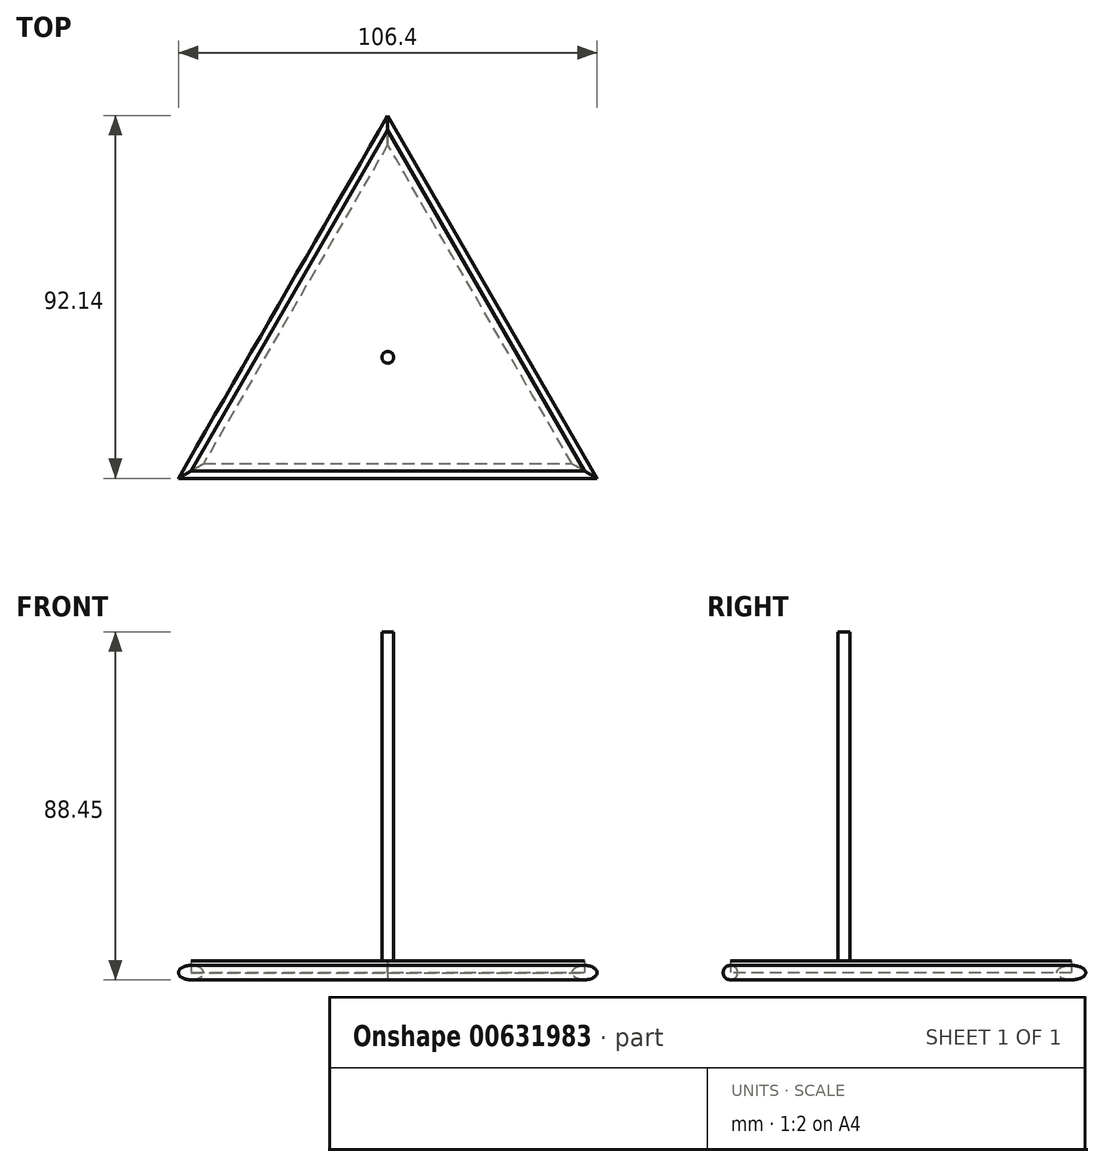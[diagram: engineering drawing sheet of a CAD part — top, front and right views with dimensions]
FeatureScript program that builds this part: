
annotation { "Feature Type Name" : "Feature", "Feature Type Description" : "" }
export const myFeature = defineFeature(function(context is Context, id is Id, definition is map)
    precondition{}
    {
        {
            var Q0;
            Q0=qCreatedBy(makeId("Top.planeOp"),FACE);
            var sketch = newSketch(context, id + "F0", { "sketchPlane" : qUnion([Q0])});
            skCircle(sketch, "E0.cCircle", {"center": v(0, 0) * mm, "radius": 28.87 * mm, "construction": true});
            skLineSegment(sketch, "E0.0", {"start": v(50, -28.87) * mm, "end": v(-50, -28.87) * mm});
            skLineSegment(sketch, "E0.1", {"start": v(-50, -28.87) * mm, "end": v(0, 57.74) * mm});
            skLineSegment(sketch, "E0.2", {"start": v(0, 57.74) * mm, "end": v(50, -28.87) * mm});
            skPoint(sketch, "E0.0.midPoint", {"position": v(0, -28.87) * mm});
            skCircle(sketch, "E1", {"center": v(0, 0) * mm, "radius": 1.5 * mm});
            skSolve(sketch);
        }
        {
            var Q0;
            Q0=makeQuery(id+"F0.imprint","IMPRINT",FACE,{"disambiguationData":[TD([[makeQuery(id+"F0.imprint","IMPRINT",EDGE,{"derivedFrom":sQuery(id+"F0.wireOp",EDGE,"E1")}),1.0]])]});
            extrude(context, id + "F1", {"entities" : qUnion([Q0]), "depth" : 86.6 * mm, "offsetDistance" : 25 * mm});
        }
        {
            var Q0;
            Q0=makeQuery(id+"F0.imprint","IMPRINT",FACE,{"disambiguationData":[TD([[makeQuery(id+"F0.imprint","IMPRINT",EDGE,{"derivedFrom":sQuery(id+"F0.wireOp",EDGE,"E0.0")}),-1.0]])]});
            extrude(context, id + "F2", {"entities" : qUnion([Q0]), "operationType" : NewBodyOperationType.ADD, "depth" : 3 * mm, "offsetDistance" : 25 * mm});
        }
        {
            var Q0;
            Q0=qCreatedBy(makeId("Right.planeOp"),FACE);
            var sketch = newSketch(context, id + "F3", { "sketchPlane" : qUnion([Q0])});
            skLineSegment(sketch, "E2.0", {"start": v(-28.87, 3) * mm, "end": v(-28.87, 0) * mm});
            skCircle(sketch, "E3", {"center": v(-28.87, 0) * mm, "radius": 1.85 * mm});
            skSolve(sketch);
        }
        {
            var Q0;
            Q0=makeQuery(id+"F3.imprint","IMPRINT",FACE,{"disambiguationData":[TD([[makeQuery(id+"F3.imprint","IMPRINT",EDGE,{"derivedFrom":sQuery(id+"F3.wireOp",EDGE,"E3")}),1.0]])]});
            var Q1;
            Q1=sQuery(id+"F0.wireOp",EDGE,"E0.0");
            var Q2;
            Q2=sQuery(id+"F0.wireOp",EDGE,"E0.1");
            var Q3;
            Q3=sQuery(id+"F0.wireOp",EDGE,"E0.2");
            sweep(context, id + "F4", {"profiles" : qUnion([Q0]), "path" : qUnion([Q1, Q2, Q3])});
        }
    });
